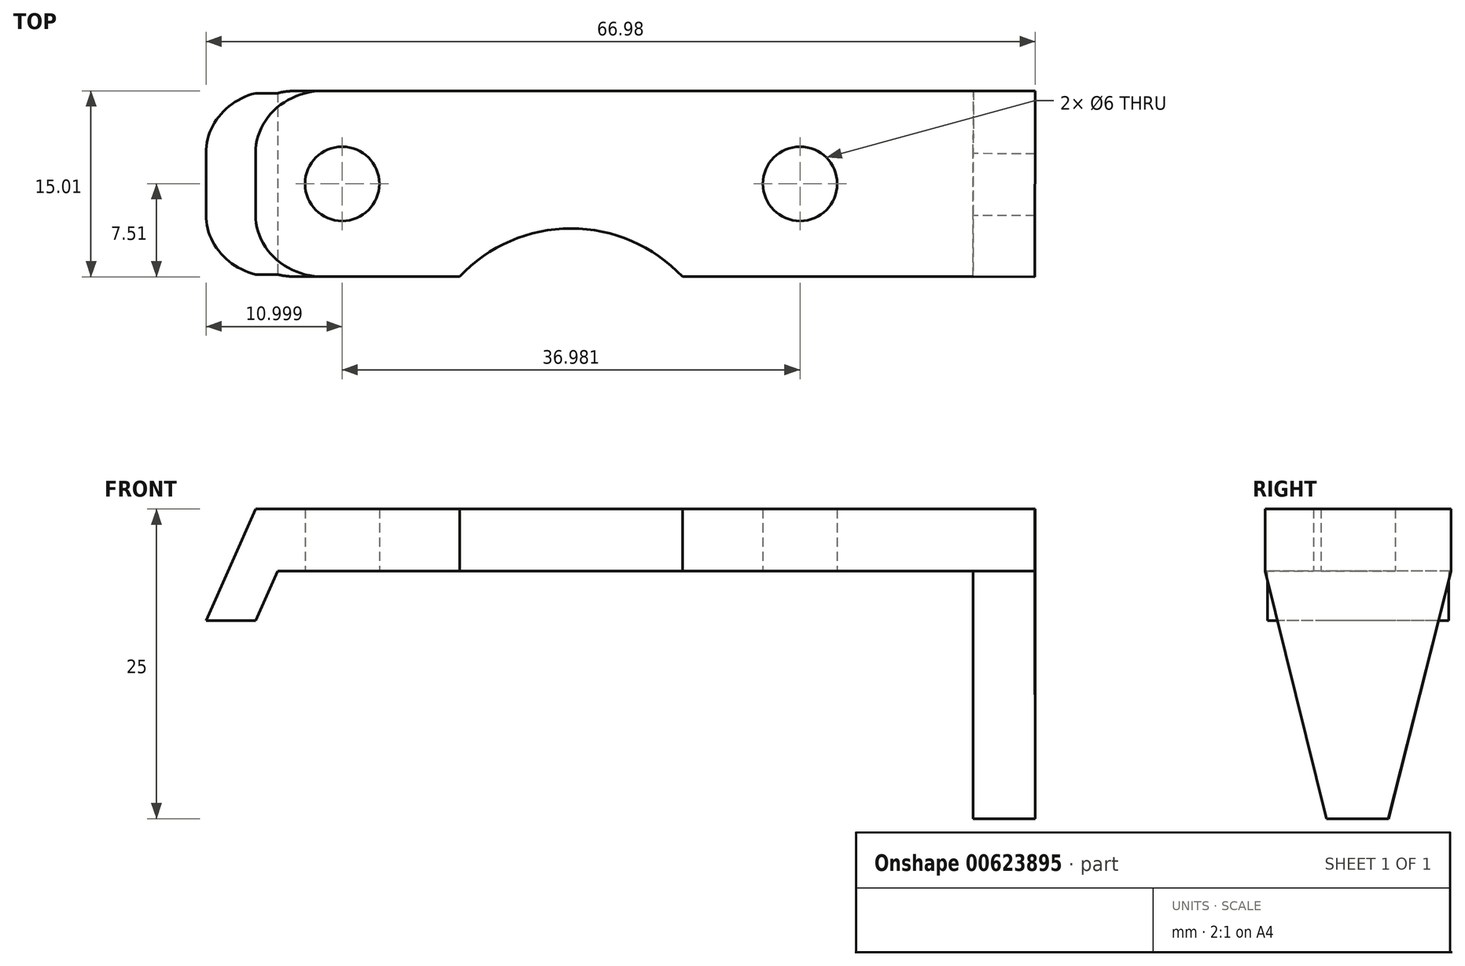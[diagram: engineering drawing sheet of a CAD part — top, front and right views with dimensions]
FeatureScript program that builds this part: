
annotation { "Feature Type Name" : "Feature", "Feature Type Description" : "" }
export const myFeature = defineFeature(function(context is Context, id is Id, definition is map)
    precondition{}
    {
        {
            var Q0;
            Q0=qCreatedBy(makeId("Top.planeOp"),FACE);
            var sketch = newSketch(context, id + "F0", { "sketchPlane" : qUnion([Q0])});
            skCircle(sketch, "E0", {"center": v(-18.48, 0) * mm, "radius": 3 * mm});
            skCircle(sketch, "E1", {"center": v(18.5, 0) * mm, "radius": 3 * mm});
            skLineSegment(sketch, "E2", {"start": v(32.5, 7.5) * mm, "end": v(32.47, -7.5) * mm});
            skLineSegment(sketch, "E3.right", {"start": v(-25.48, 0) * mm, "end": v(-25.48, 7.5) * mm});
            skLineSegment(sketch, "E4", {"start": v(-25.48, 7.5) * mm, "end": v(-25.48, -7.5) * mm});
            skLineSegment(sketch, "E5", {"start": v(-25.48, 7.5) * mm, "end": v(32.5, 7.5) * mm});
            skArc(sketch, "E6", {"start": v(9, -7.5) * mm, "mid": v(0, -3.6) * mm, "end": v(-9, -7.5) * mm});
            skLineSegment(sketch, "E7", {"start": v(-25.48, -7.5) * mm, "end": v(-9, -7.5) * mm});
            skLineSegment(sketch, "E8", {"start": v(9, -7.5) * mm, "end": v(32.47, -7.5) * mm});
            skSolve(sketch);
        }
        {
            var Q0;
            Q0=makeQuery(id+"F0.imprint","IMPRINT",FACE,{"disambiguationData":[TD([[makeQuery(id+"F0.imprint","IMPRINT",EDGE,{"derivedFrom":sQuery(id+"F0.wireOp",EDGE,"E0")}),-1.0]])]});
            extrude(context, id + "F1", {"entities" : qUnion([Q0]), "depth" : 5 * mm, "offsetDistance" : 25 * mm});
        }
        {
            var Q0;
            Q0=makeQuery(id+"F1.opExtrude","SWEPT_FACE",FACE,{"disambiguationData":[OSD([sQuery(id+"F0.wireOp",EDGE,"E2")])]});
            var sketch = newSketch(context, id + "F2", { "sketchPlane" : qUnion([Q0])});
            skPoint(sketch, "E9.middle", {"position": v(0, -20) * mm});
            skLineSegment(sketch, "E10", {"start": v(-7.43, 0) * mm, "end": v(-2.5, -20) * mm});
            skLineSegment(sketch, "E11", {"start": v(-2.5, -20) * mm, "end": v(2.5, -20) * mm});
            skLineSegment(sketch, "E12", {"start": v(2.5, -20) * mm, "end": v(7.57, 0) * mm});
            skSolve(sketch);
        }
        {
            var Q0;
            Q0=makeQuery(id+"F2.imprint","IMPRINT",FACE,{"disambiguationData":[TD([[makeQuery(id+"F2.imprint","IMPRINT",EDGE,{"derivedFrom":sQuery(id+"F2.wireOp",EDGE,"E10")}),1.0]])]});
            var Q1;
            {var subQ0=sQuery(id+"F0.wireOp",EDGE,"E2");Q1=makeQuery(id+"F2.imprint","IMPRINT",FACE,{"disambiguationData":[TD([[makeQuery(id+"F2.imprint","IMPRINT",EDGE,{"derivedFrom":makeQuery(id+"F1.opExtrude","CAP_EDGE",EDGE,{"disambiguationData":[OSD([subQ0])],"isStart":true})}),-1.0]])]});}
            extrude(context, id + "F3", {"entities" : qUnion([Q0, Q1]), "operationType" : NewBodyOperationType.ADD, "depth" : 5 * mm, "offsetDistance" : 25 * mm});
        }
        {
            var Q0;
            Q0=makeQuery(id+"F1.opExtrude","SWEPT_FACE",FACE,{"disambiguationData":[OSD([sQuery(id+"F0.wireOp",EDGE,"E7")])]});
            var sketch = newSketch(context, id + "F4", { "sketchPlane" : qUnion([Q0])});
            skLineSegment(sketch, "E13.top", {"start": v(-25.48, -4) * mm, "end": v(-29.48, -4) * mm});
            skLineSegment(sketch, "E14", {"start": v(-25.48, 5) * mm, "end": v(-29.48, -4) * mm});
            skLineSegment(sketch, "E15", {"start": v(-25.48, 5) * mm, "end": v(-21.48, 5) * mm});
            skLineSegment(sketch, "E16", {"start": v(-21.48, 5) * mm, "end": v(-25.48, -4) * mm});
            skSolve(sketch);
        }
        {
            var Q0;
            {var subQ1=sQuery(id+"F4.wireOp",EDGE,"E13.top");Q0=makeQuery(id+"F4.imprint","IMPRINT",FACE,{"disambiguationData":[TD([[makeQuery(id+"F4.imprint","IMPRINT",EDGE,{"derivedFrom":subQ1}),-1.0]])]});}
            var Q1;
            {var subQ0=sQuery(id+"F4.wireOp",EDGE,"E15");Q1=makeQuery(id+"F4.imprint","IMPRINT",FACE,{"disambiguationData":[TD([[makeQuery(id+"F4.imprint","IMPRINT",EDGE,{"derivedFrom":subQ0}),-1.0]])]});}
            extrude(context, id + "F5", {"entities" : qUnion([Q0, Q1]), "operationType" : NewBodyOperationType.ADD, "oppositeDirection" : true, "depth" : 15 * mm, "offsetDistance" : 25 * mm});
        }
        {
            var Q0;
            Q0=makeQuery(id+"F5.opExtrude","CAP_EDGE",EDGE,{"disambiguationData":[OSD([sQuery(id+"F4.wireOp",EDGE,"E14")])],"isStart":true});
            var Q1;
            Q1=makeQuery(id+"F5.opExtrude","CAP_EDGE",EDGE,{"disambiguationData":[OSD([sQuery(id+"F4.wireOp",EDGE,"E14")])],"isStart":false});
            fillet(context, id + "F6", {"entities" : qUnion([Q0, Q1]), "radius" : 5 * mm, "tangentPropagation" : true, "allowEdgeOverflow" : false});
        }
    });
